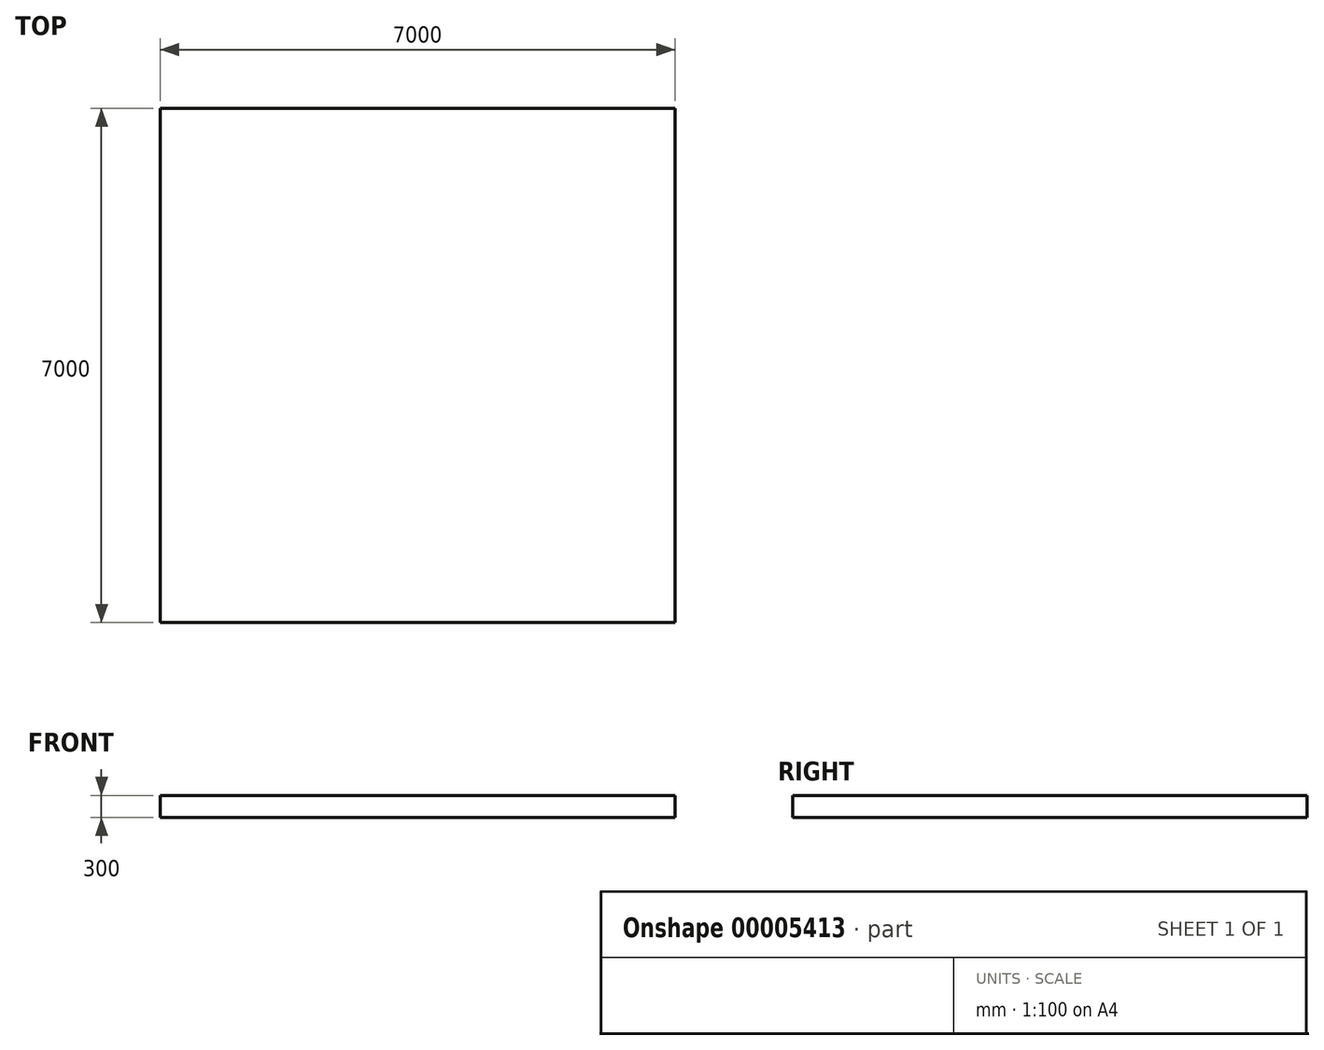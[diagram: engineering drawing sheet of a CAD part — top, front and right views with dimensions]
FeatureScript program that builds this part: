
annotation { "Feature Type Name" : "Feature", "Feature Type Description" : "" }
export const myFeature = defineFeature(function(context is Context, id is Id, definition is map)
    precondition{}
    {
        {
            var Q0;
            Q0=qCreatedBy(makeId("Top.planeOp"),FACE);
            var sketch = newSketch(context, id + "F0", { "sketchPlane" : qUnion([Q0])});
            skLineSegment(sketch, "E0.bottom", {"start": v(0, 2468.81) * mm, "end": v(7000, 2468.81) * mm});
            skLineSegment(sketch, "E0.top", {"start": v(0, -4531.19) * mm, "end": v(7000, -4531.19) * mm});
            skLineSegment(sketch, "E0.left", {"start": v(0, 2468.81) * mm, "end": v(0, -4531.19) * mm});
            skLineSegment(sketch, "E0.right", {"start": v(7000, 2468.81) * mm, "end": v(7000, -4531.19) * mm});
            skSolve(sketch);
        }
        {
            var Q0;
            Q0 = qSketchRegion(id + "F0", true);
            extrude(context, id + "F1", {"entities" : qUnion([Q0]), "depth" : 300 * mm});
        }
    });
